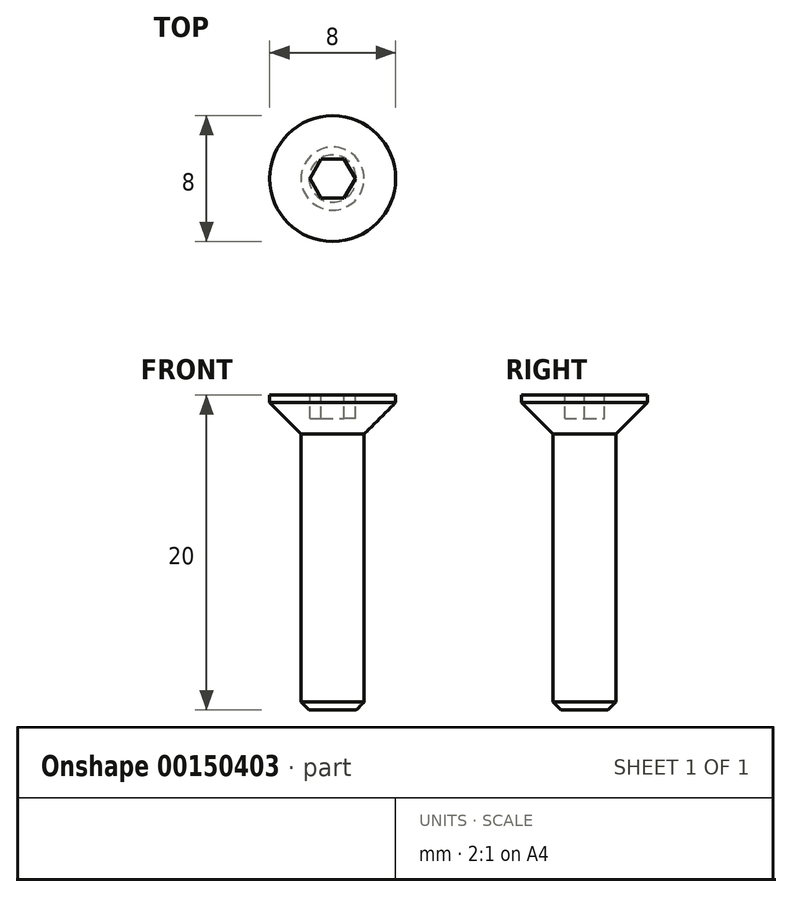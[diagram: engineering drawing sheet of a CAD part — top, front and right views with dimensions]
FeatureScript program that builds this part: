
annotation { "Feature Type Name" : "Feature", "Feature Type Description" : "" }
export const myFeature = defineFeature(function(context is Context, id is Id, definition is map)
    precondition{}
    {
        {
            var Q0;
            Q0=qCreatedBy(makeId("Front.planeOp"),FACE);
            var sketch = newSketch(context, id + "F0", { "sketchPlane" : qUnion([Q0])});
            skLineSegment(sketch, "E0", {"start": v(0, 0) * mm, "end": v(4.48, 0) * mm});
            skLineSegment(sketch, "E1", {"start": v(4.48, 0) * mm, "end": v(0, -4.48) * mm});
            skLineSegment(sketch, "E2", {"start": v(0, 0) * mm, "end": v(0, -4.48) * mm, "construction": true});
            skLineSegment(sketch, "E3", {"start": v(0, 0) * mm, "end": v(0, -20) * mm});
            skLineSegment(sketch, "E4", {"start": v(0, -20) * mm, "end": v(2, -20) * mm});
            skLineSegment(sketch, "E5", {"start": v(2, -20) * mm, "end": v(2, -2.48) * mm});
            skSolve(sketch);
        }
        {
            var Q0;
            {var subQ0=sQuery(id+"F0.wireOp",EDGE,"E0");Q0=makeQuery(id+"F0.imprint","IMPRINT",FACE,{"disambiguationData":[TD([[makeQuery(id+"F0.imprint","IMPRINT",EDGE,{"derivedFrom":subQ0}),-1.0]])]});}
            var Q1;
            {var subQ4=sQuery(id+"F0.wireOp",EDGE,"E4");Q1=makeQuery(id+"F0.imprint","IMPRINT",FACE,{"disambiguationData":[TD([[makeQuery(id+"F0.imprint","IMPRINT",EDGE,{"derivedFrom":subQ4}),1.0]])]});}
            var Q2;
            Q2=sQuery(id+"F0.wireOp",EDGE,"E3");
            revolve(context, id + "F1", {"entities" : qUnion([Q0, Q1]), "axis" : qUnion([Q2]), "revolveType" : RevolveType.FULL});
        }
        {
            var Q0;
            Q0=makeQuery(id+"F1.opRevolve","SWEPT_EDGE",EDGE,{"disambiguationData":[OSD([sQuery(id+"F0.wireOp",EDGE,"E4"),sQuery(id+"F0.wireOp",EDGE,"E5")])]});
            chamfer(context, id + "F2", {"entities" : qUnion([Q0]), "width" : 0.5 * mm, "tangentPropagation" : true});
        }
        {
            var Q0;
            Q0=qCreatedBy(makeId("Top.planeOp"),FACE);
            var sketch = newSketch(context, id + "F3", { "sketchPlane" : qUnion([Q0])});
            skCircle(sketch, "E6", {"center": v(0, 0) * mm, "radius": 4 * mm});
            skCircle(sketch, "E7.0", {"center": v(0, 0) * mm, "radius": 4.48 * mm});
            skCircle(sketch, "E8.cCircle", {"center": v(0, 0) * mm, "radius": 1.25 * mm, "construction": true});
            skLineSegment(sketch, "E8.0", {"start": v(-0.72, 1.25) * mm, "end": v(0.72, 1.25) * mm});
            skLineSegment(sketch, "E8.1", {"start": v(0.72, 1.25) * mm, "end": v(1.44, 0) * mm});
            skLineSegment(sketch, "E8.2", {"start": v(1.44, 0) * mm, "end": v(0.72, -1.25) * mm});
            skLineSegment(sketch, "E8.3", {"start": v(0.72, -1.25) * mm, "end": v(-0.72, -1.25) * mm});
            skLineSegment(sketch, "E8.4", {"start": v(-0.72, -1.25) * mm, "end": v(-1.44, 0) * mm});
            skLineSegment(sketch, "E8.5", {"start": v(-1.44, 0) * mm, "end": v(-0.72, 1.25) * mm});
            skPoint(sketch, "E8.0.midPoint", {"position": v(0, 1.25) * mm});
            skSolve(sketch);
        }
        {
            var Q0;
            Q0=makeQuery(id+"F3.imprint","IMPRINT",FACE,{"disambiguationData":[TD([[makeQuery(id+"F3.imprint","IMPRINT",EDGE,{"derivedFrom":sQuery(id+"F3.wireOp",EDGE,"E8.0")}),-1.0]])]});
            var Q1;
            Q1=makeQuery(id+"F3.imprint","IMPRINT",FACE,{"disambiguationData":[TD([[makeQuery(id+"F3.imprint","IMPRINT",EDGE,{"derivedFrom":sQuery(id+"F3.wireOp",EDGE,"E6")}),-1.0]])]});
            extrude(context, id + "F4", {"entities" : qUnion([Q0, Q1]), "operationType" : NewBodyOperationType.REMOVE, "oppositeDirection" : true, "depth" : 1.49 * mm});
        }
    });
